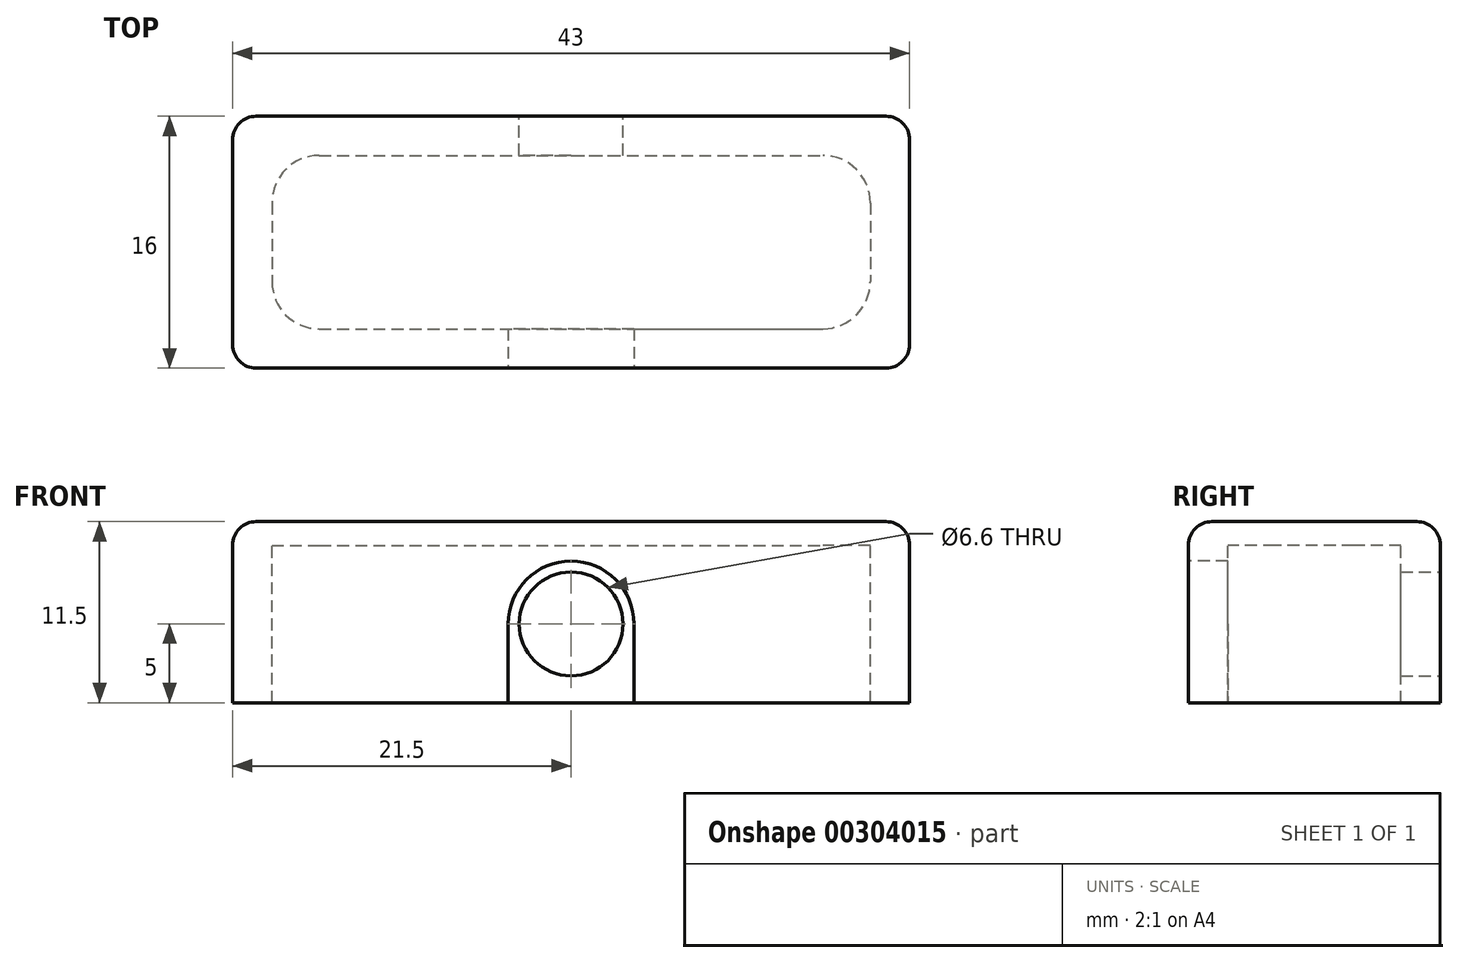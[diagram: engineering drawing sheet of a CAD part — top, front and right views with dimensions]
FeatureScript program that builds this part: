
annotation { "Feature Type Name" : "Feature", "Feature Type Description" : "" }
export const myFeature = defineFeature(function(context is Context, id is Id, definition is map)
    precondition{}
    {
        {
            var Q0;
            Q0=qCreatedBy(makeId("Top.planeOp"),FACE);
            var sketch = newSketch(context, id + "F0", { "sketchPlane" : qUnion([Q0])});
            skLineSegment(sketch, "E0.bottom", {"start": v(-43, 0) * mm, "end": v(0, 0) * mm});
            skLineSegment(sketch, "E0.top", {"start": v(-43, -16) * mm, "end": v(0, -16) * mm});
            skLineSegment(sketch, "E0.left", {"start": v(-43, 0) * mm, "end": v(-43, -16) * mm});
            skLineSegment(sketch, "E0.right", {"start": v(0, 0) * mm, "end": v(0, -16) * mm});
            skLineSegment(sketch, "E1.bottom", {"start": v(-40.5, -2.5) * mm, "end": v(-2.5, -2.5) * mm});
            skLineSegment(sketch, "E1.top", {"start": v(-40.5, -13.5) * mm, "end": v(-2.5, -13.5) * mm});
            skLineSegment(sketch, "E1.left", {"start": v(-40.5, -2.5) * mm, "end": v(-40.5, -13.5) * mm});
            skLineSegment(sketch, "E1.right", {"start": v(-2.5, -2.5) * mm, "end": v(-2.5, -13.5) * mm});
            skSolve(sketch);
        }
        {
            var Q0;
            Q0=makeQuery(id+"F0.imprint","IMPRINT",FACE,{"disambiguationData":[TD([[makeQuery(id+"F0.imprint","IMPRINT",EDGE,{"derivedFrom":sQuery(id+"F0.wireOp",EDGE,"E0.bottom")}),-1.0]])]});
            var Q1;
            Q1=makeQuery(id+"F0.imprint","IMPRINT",FACE,{"disambiguationData":[TD([[makeQuery(id+"F0.imprint","IMPRINT",EDGE,{"derivedFrom":sQuery(id+"F0.wireOp",EDGE,"E1.bottom")}),-1.0]])]});
            extrude(context, id + "F1", {"entities" : qUnion([Q0, Q1]), "depth" : 1.5 * mm});
        }
        {
            var Q0;
            Q0=makeQuery(id+"F0.imprint","IMPRINT",FACE,{"disambiguationData":[TD([[makeQuery(id+"F0.imprint","IMPRINT",EDGE,{"derivedFrom":sQuery(id+"F0.wireOp",EDGE,"E0.bottom")}),-1.0]])]});
            extrude(context, id + "F2", {"entities" : qUnion([Q0]), "operationType" : NewBodyOperationType.ADD, "oppositeDirection" : true, "depth" : 10 * mm});
        }
        {
            var Q0;
            {var subQ0=sQuery(id+"F0.wireOp",EDGE,"E0.bottom");Q0=makeQuery(id+"F2.boolean.opBoolean","MERGE",FACE,{"derivedFrom":[makeQuery(id+"F1.opExtrude","SWEPT_FACE",FACE,{"disambiguationData":[OSD([subQ0])]}),makeQuery(id+"F2.opExtrude","SWEPT_FACE",FACE,{"disambiguationData":[OSD([subQ0])]})]});}
            var sketch = newSketch(context, id + "F3", { "sketchPlane" : qUnion([Q0])});
            skPoint(sketch, "E2", {"position": v(21.5, -5) * mm});
            skPoint(sketch, "E2.positionSnap0", {"position": v(21.5, -10) * mm});
            skSolve(sketch);
        }
        {
            var Q0;
            Q0=sQuery(id+"F3.wireOp",VERTEX,"E2");
            var Q1;
            Q1=makeQuery(id+"F1.opExtrude","SWEPT_BODY",BODY,{"disambiguationData":[OSD([sQuery(id+"F0.wireOp",EDGE,"E0.bottom"),sQuery(id+"F0.wireOp",EDGE,"E0.top"),sQuery(id+"F0.wireOp",EDGE,"E0.left"),sQuery(id+"F0.wireOp",EDGE,"E0.right")])]});
            hole(context, id + "F4", {"style" : HoleStyle.SIMPLE, "endStyle" : HoleEndStyle.BLIND, "holeDiameter" : 6.6 * mm, "holeDepth" : 3 * mm, "tappedDepth" : 12 * mm, "tapClearance" : 3, "locations" : qUnion([Q0]), "scope" : qUnion([Q1])});
        }
        {
            var Q0;
            {var subQ0=sQuery(id+"F0.wireOp",EDGE,"E0.right");var subQ1=sQuery(id+"F0.wireOp",EDGE,"E0.bottom");Q0=makeQuery(id+"F2.boolean.opBoolean","MERGE",EDGE,{"derivedFrom":[makeQuery(id+"F1.opExtrude","SWEPT_EDGE",EDGE,{"disambiguationData":[OSD([subQ1,subQ0])]}),makeQuery(id+"F2.opExtrude","SWEPT_EDGE",EDGE,{"disambiguationData":[OSD([subQ1,subQ0])]})]});}
            var Q1;
            {var subQ0=sQuery(id+"F0.wireOp",EDGE,"E0.right");var subQ1=sQuery(id+"F0.wireOp",EDGE,"E0.top");Q1=makeQuery(id+"F2.boolean.opBoolean","MERGE",EDGE,{"derivedFrom":[makeQuery(id+"F1.opExtrude","SWEPT_EDGE",EDGE,{"disambiguationData":[OSD([subQ1,subQ0])]}),makeQuery(id+"F2.opExtrude","SWEPT_EDGE",EDGE,{"disambiguationData":[OSD([subQ1,subQ0])]})]});}
            var Q2;
            {var subQ0=sQuery(id+"F0.wireOp",EDGE,"E0.left");var subQ1=sQuery(id+"F0.wireOp",EDGE,"E0.top");Q2=makeQuery(id+"F2.boolean.opBoolean","MERGE",EDGE,{"derivedFrom":[makeQuery(id+"F1.opExtrude","SWEPT_EDGE",EDGE,{"disambiguationData":[OSD([subQ1,subQ0])]}),makeQuery(id+"F2.opExtrude","SWEPT_EDGE",EDGE,{"disambiguationData":[OSD([subQ1,subQ0])]})]});}
            var Q3;
            {var subQ0=sQuery(id+"F0.wireOp",EDGE,"E0.left");var subQ1=sQuery(id+"F0.wireOp",EDGE,"E0.bottom");Q3=makeQuery(id+"F2.boolean.opBoolean","MERGE",EDGE,{"derivedFrom":[makeQuery(id+"F1.opExtrude","SWEPT_EDGE",EDGE,{"disambiguationData":[OSD([subQ1,subQ0])]}),makeQuery(id+"F2.opExtrude","SWEPT_EDGE",EDGE,{"disambiguationData":[OSD([subQ1,subQ0])]})]});}
            var Q4;
            Q4=makeQuery(id+"F1.opExtrude","CAP_EDGE",EDGE,{"disambiguationData":[OSD([sQuery(id+"F0.wireOp",EDGE,"E0.bottom")])],"isStart":false});
            var Q5;
            Q5=makeQuery(id+"F1.opExtrude","CAP_EDGE",EDGE,{"disambiguationData":[OSD([sQuery(id+"F0.wireOp",EDGE,"E0.left")])],"isStart":false});
            var Q6;
            Q6=makeQuery(id+"F1.opExtrude","CAP_EDGE",EDGE,{"disambiguationData":[OSD([sQuery(id+"F0.wireOp",EDGE,"E0.top")])],"isStart":false});
            var Q7;
            Q7=makeQuery(id+"F1.opExtrude","CAP_EDGE",EDGE,{"disambiguationData":[OSD([sQuery(id+"F0.wireOp",EDGE,"E0.right")])],"isStart":false});
            fillet(context, id + "F5", {"entities" : qUnion([Q0, Q1, Q2, Q3, Q4, Q5, Q6, Q7]), "radius" : 1.5 * mm, "tangentPropagation" : true, "allowEdgeOverflow" : false});
        }
        {
            var Q0;
            Q0=makeQuery(id+"F2.opExtrude","SWEPT_EDGE",EDGE,{"disambiguationData":[OSD([sQuery(id+"F0.wireOp",EDGE,"E1.bottom"),sQuery(id+"F0.wireOp",EDGE,"E1.right")])]});
            var Q1;
            Q1=makeQuery(id+"F2.opExtrude","SWEPT_EDGE",EDGE,{"disambiguationData":[OSD([sQuery(id+"F0.wireOp",EDGE,"E1.bottom"),sQuery(id+"F0.wireOp",EDGE,"E1.left")])]});
            var Q2;
            Q2=makeQuery(id+"F2.opExtrude","SWEPT_EDGE",EDGE,{"disambiguationData":[OSD([sQuery(id+"F0.wireOp",EDGE,"E1.top"),sQuery(id+"F0.wireOp",EDGE,"E1.right")])]});
            var Q3;
            Q3=makeQuery(id+"F2.opExtrude","SWEPT_EDGE",EDGE,{"disambiguationData":[OSD([sQuery(id+"F0.wireOp",EDGE,"E1.top"),sQuery(id+"F0.wireOp",EDGE,"E1.left")])]});
            fillet(context, id + "F6", {"entities" : qUnion([Q0, Q1, Q2, Q3]), "radius" : 3 * mm, "tangentPropagation" : true, "allowEdgeOverflow" : false});
        }
        {
            var Q0;
            {var subQ0=sQuery(id+"F0.wireOp",EDGE,"E0.top");Q0=makeQuery(id+"F2.boolean.opBoolean","MERGE",FACE,{"derivedFrom":[makeQuery(id+"F1.opExtrude","SWEPT_FACE",FACE,{"disambiguationData":[OSD([subQ0])]}),makeQuery(id+"F2.opExtrude","SWEPT_FACE",FACE,{"disambiguationData":[OSD([subQ0])]})]});}
            var sketch = newSketch(context, id + "F7", { "sketchPlane" : qUnion([Q0])});
            skPoint(sketch, "E3", {"position": v(-21.5, -5) * mm});
            skPoint(sketch, "E3.positionSnap0", {"position": v(-21.5, -10) * mm});
            skSolve(sketch);
        }
        {
            var Q0;
            Q0=sQuery(id+"F7.wireOp",VERTEX,"E3");
            var Q1;
            Q1=makeQuery(id+"F1.opExtrude","SWEPT_BODY",BODY,{"disambiguationData":[OSD([sQuery(id+"F0.wireOp",EDGE,"E0.bottom"),sQuery(id+"F0.wireOp",EDGE,"E0.top"),sQuery(id+"F0.wireOp",EDGE,"E0.left"),sQuery(id+"F0.wireOp",EDGE,"E0.right")])]});
            hole(context, id + "F8", {"style" : HoleStyle.SIMPLE, "endStyle" : HoleEndStyle.BLIND, "holeDiameter" : 8 * mm, "holeDepth" : 3 * mm, "tappedDepth" : 12 * mm, "tapClearance" : 3, "locations" : qUnion([Q0]), "scope" : qUnion([Q1])});
        }
        {
            var Q0;
            {var subQ0=sQuery(id+"F0.wireOp",EDGE,"E0.top");Q0=makeQuery(id+"F2.boolean.opBoolean","MERGE",FACE,{"derivedFrom":[makeQuery(id+"F1.opExtrude","SWEPT_FACE",FACE,{"disambiguationData":[OSD([subQ0])]}),makeQuery(id+"F2.opExtrude","SWEPT_FACE",FACE,{"disambiguationData":[OSD([subQ0])]})]});}
            var sketch = newSketch(context, id + "F9", { "sketchPlane" : qUnion([Q0])});
            skLineSegment(sketch, "E4", {"start": v(-25.5, -10) * mm, "end": v(-25.5, -5) * mm});
            skLineSegment(sketch, "E5", {"start": v(-17.5, -10) * mm, "end": v(-17.5, -5) * mm});
            skLineSegment(sketch, "E6", {"start": v(-25.5, -10) * mm, "end": v(-17.5, -10) * mm});
            skLineSegment(sketch, "E7", {"start": v(-25.5, -5) * mm, "end": v(-17.5, -5) * mm});
            skSolve(sketch);
        }
        {
            var Q0;
            {var subQ0=sQuery(id+"F9.wireOp",EDGE,"E4");Q0=makeQuery(id+"F9.imprint","IMPRINT",FACE,{"disambiguationData":[TD([[makeQuery(id+"F9.imprint","IMPRINT",EDGE,{"derivedFrom":subQ0}),-1.0]])]});}
            extrude(context, id + "F10", {"entities" : qUnion([Q0]), "operationType" : NewBodyOperationType.REMOVE, "endBound" : BoundingType.UP_TO_NEXT, "oppositeDirection" : true, "depth" : 25 * mm});
        }
    });
